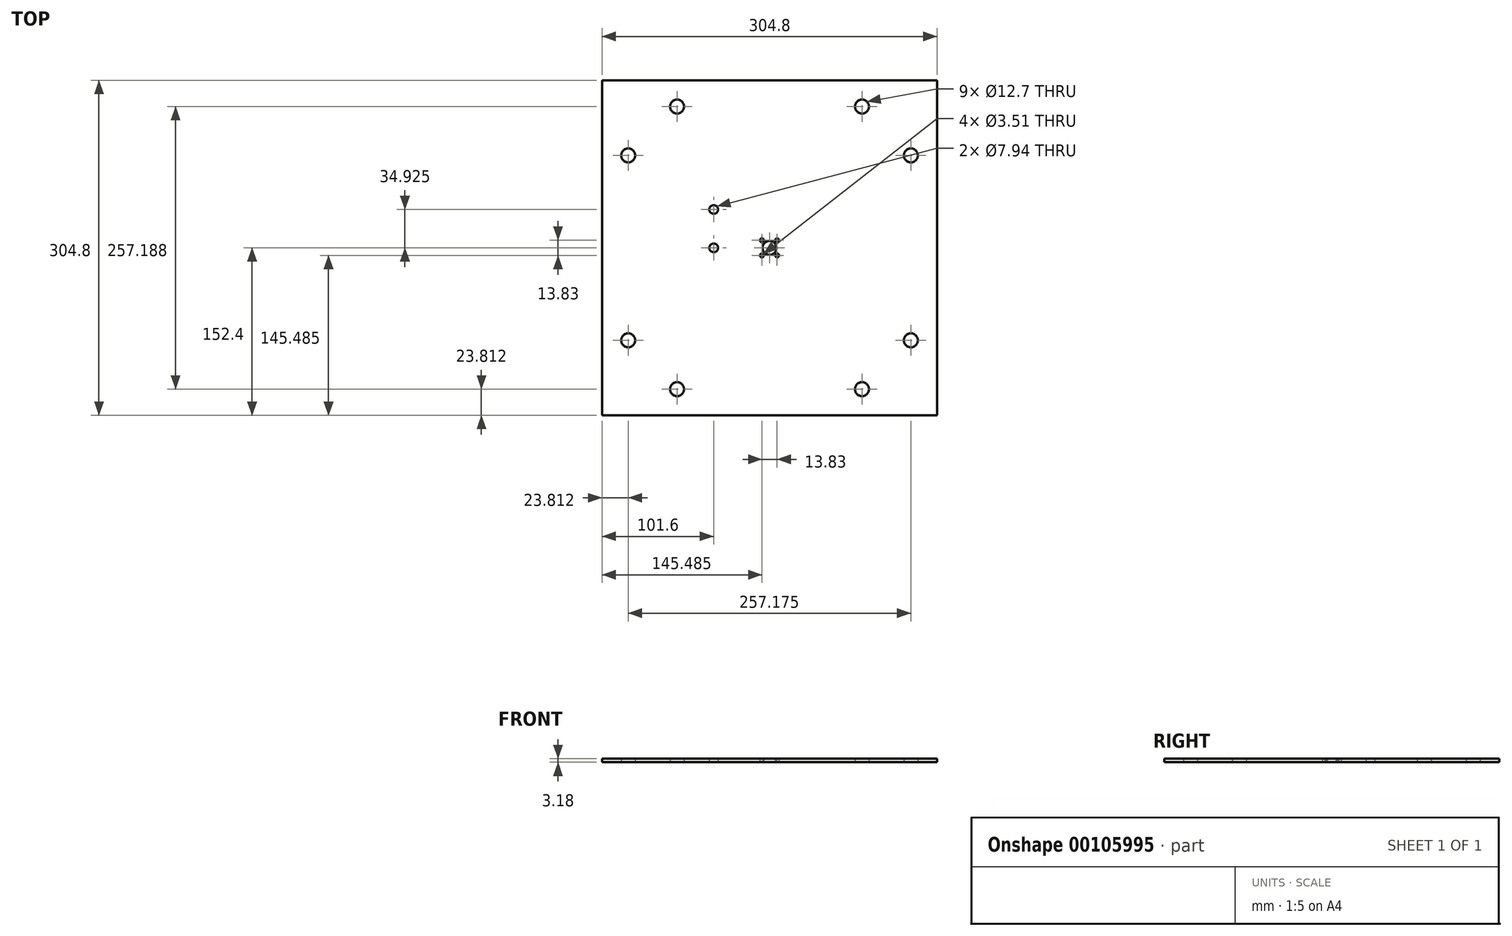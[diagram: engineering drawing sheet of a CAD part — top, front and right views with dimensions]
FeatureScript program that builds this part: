
annotation { "Feature Type Name" : "Feature", "Feature Type Description" : "" }
export const myFeature = defineFeature(function(context is Context, id is Id, definition is map)
    precondition{}
    {
        {
            var Q0;
            Q0=qCreatedBy(makeId("Top.planeOp"),FACE);
            var sketch = newSketch(context, id + "F0", { "sketchPlane" : qUnion([Q0])});
            skLineSegment(sketch, "E0.bottom", {"start": v(-152.4, 152.4) * mm, "end": v(152.4, 152.4) * mm});
            skLineSegment(sketch, "E0.top", {"start": v(-152.4, -152.4) * mm, "end": v(152.4, -152.4) * mm});
            skLineSegment(sketch, "E0.left", {"start": v(-152.4, 152.4) * mm, "end": v(-152.4, -152.4) * mm});
            skLineSegment(sketch, "E0.right", {"start": v(152.4, 152.4) * mm, "end": v(152.4, -152.4) * mm});
            skCircle(sketch, "E1", {"center": v(0, 0) * mm, "radius": 6.35 * mm});
            skLineSegment(sketch, "E2.bottom", {"start": v(-8.98, 8.98) * mm, "end": v(8.98, 8.98) * mm, "construction": true});
            skLineSegment(sketch, "E2.top", {"start": v(-8.98, -8.98) * mm, "end": v(8.98, -8.98) * mm, "construction": true});
            skLineSegment(sketch, "E2.left", {"start": v(-8.98, 8.98) * mm, "end": v(-8.98, -8.98) * mm, "construction": true});
            skLineSegment(sketch, "E2.right", {"start": v(8.98, 8.98) * mm, "end": v(8.98, -8.98) * mm, "construction": true});
            skLineSegment(sketch, "E3", {"start": v(0, 8.98) * mm, "end": v(0, -8.98) * mm, "construction": true});
            skLineSegment(sketch, "E4", {"start": v(-8.98, 0) * mm, "end": v(8.98, 0) * mm, "construction": true});
            skLineSegment(sketch, "E5.bottom", {"start": v(-6.91, 6.91) * mm, "end": v(6.91, 6.91) * mm, "construction": true});
            skLineSegment(sketch, "E5.top", {"start": v(-6.91, -6.91) * mm, "end": v(6.91, -6.91) * mm, "construction": true});
            skLineSegment(sketch, "E5.left", {"start": v(-6.91, 6.91) * mm, "end": v(-6.91, -6.91) * mm, "construction": true});
            skLineSegment(sketch, "E5.right", {"start": v(6.91, 6.91) * mm, "end": v(6.91, -6.91) * mm, "construction": true});
            skLineSegment(sketch, "E6", {"start": v(0, 6.91) * mm, "end": v(0, -6.91) * mm, "construction": true});
            skLineSegment(sketch, "E7", {"start": v(-6.91, 0) * mm, "end": v(6.91, 0) * mm, "construction": true});
            skCircle(sketch, "E8", {"center": v(-6.91, 6.91) * mm, "radius": 1.75 * mm});
            skCircle(sketch, "E9", {"center": v(6.91, 6.91) * mm, "radius": 1.75 * mm});
            skCircle(sketch, "E10", {"center": v(6.91, -6.91) * mm, "radius": 1.75 * mm});
            skCircle(sketch, "E11", {"center": v(-6.91, -6.91) * mm, "radius": 1.75 * mm});
            skLineSegment(sketch, "E12.bottom", {"start": v(-152.4, 152.4) * mm, "end": v(-128.59, 152.4) * mm, "construction": true});
            skLineSegment(sketch, "E12.top", {"start": v(-152.4, 128.59) * mm, "end": v(-128.59, 128.59) * mm, "construction": true});
            skLineSegment(sketch, "E12.left", {"start": v(-152.4, 152.4) * mm, "end": v(-152.4, 128.59) * mm, "construction": true});
            skLineSegment(sketch, "E12.right", {"start": v(-128.59, 152.4) * mm, "end": v(-128.59, 128.59) * mm, "construction": true});
            skLineSegment(sketch, "E13.bottom", {"start": v(152.4, 152.4) * mm, "end": v(128.59, 152.4) * mm, "construction": true});
            skLineSegment(sketch, "E13.top", {"start": v(152.4, 128.6) * mm, "end": v(128.59, 128.6) * mm, "construction": true});
            skLineSegment(sketch, "E13.left", {"start": v(152.4, 152.4) * mm, "end": v(152.4, 128.6) * mm, "construction": true});
            skLineSegment(sketch, "E13.right", {"start": v(128.59, 152.4) * mm, "end": v(128.59, 128.6) * mm, "construction": true});
            skLineSegment(sketch, "E14.bottom", {"start": v(152.4, -152.4) * mm, "end": v(128.59, -152.4) * mm, "construction": true});
            skLineSegment(sketch, "E14.top", {"start": v(152.4, -128.59) * mm, "end": v(128.59, -128.59) * mm, "construction": true});
            skLineSegment(sketch, "E14.left", {"start": v(152.4, -152.4) * mm, "end": v(152.4, -128.59) * mm, "construction": true});
            skLineSegment(sketch, "E14.right", {"start": v(128.59, -152.4) * mm, "end": v(128.59, -128.59) * mm, "construction": true});
            skLineSegment(sketch, "E15.bottom", {"start": v(-152.4, -152.4) * mm, "end": v(-128.59, -152.4) * mm, "construction": true});
            skLineSegment(sketch, "E15.top", {"start": v(-152.4, -128.59) * mm, "end": v(-128.59, -128.59) * mm, "construction": true});
            skLineSegment(sketch, "E15.left", {"start": v(-152.4, -152.4) * mm, "end": v(-152.4, -128.59) * mm, "construction": true});
            skLineSegment(sketch, "E15.right", {"start": v(-128.59, -152.4) * mm, "end": v(-128.59, -128.59) * mm, "construction": true});
            skLineSegment(sketch, "E16", {"start": v(-128.59, 152.4) * mm, "end": v(-128.59, 84.14) * mm, "construction": true});
            skLineSegment(sketch, "E17", {"start": v(-152.4, 128.59) * mm, "end": v(-84.14, 128.59) * mm, "construction": true});
            skLineSegment(sketch, "E18", {"start": v(152.4, 128.6) * mm, "end": v(84.14, 128.6) * mm, "construction": true});
            skLineSegment(sketch, "E19", {"start": v(128.59, 152.4) * mm, "end": v(128.59, 84.14) * mm, "construction": true});
            skLineSegment(sketch, "E20", {"start": v(128.59, -152.4) * mm, "end": v(128.59, -84.14) * mm, "construction": true});
            skLineSegment(sketch, "E21", {"start": v(152.4, -128.59) * mm, "end": v(84.13, -128.59) * mm, "construction": true});
            skLineSegment(sketch, "E22", {"start": v(-152.4, -128.59) * mm, "end": v(-84.14, -128.59) * mm, "construction": true});
            skLineSegment(sketch, "E23", {"start": v(-128.59, -152.4) * mm, "end": v(-128.59, -84.14) * mm, "construction": true});
            skCircle(sketch, "E24", {"center": v(-128.59, -84.14) * mm, "radius": 6.35 * mm, "construction": true});
            skCircle(sketch, "E25", {"center": v(-84.14, -128.59) * mm, "radius": 6.35 * mm, "construction": true});
            skCircle(sketch, "E26", {"center": v(-128.59, 84.14) * mm, "radius": 6.35 * mm});
            skCircle(sketch, "E27", {"center": v(-128.59, -84.14) * mm, "radius": 6.35 * mm});
            skCircle(sketch, "E28", {"center": v(-84.14, -128.59) * mm, "radius": 6.35 * mm});
            skCircle(sketch, "E29", {"center": v(84.13, -128.59) * mm, "radius": 6.35 * mm});
            skCircle(sketch, "E30", {"center": v(128.59, -84.14) * mm, "radius": 6.35 * mm});
            skCircle(sketch, "E31", {"center": v(128.59, 84.14) * mm, "radius": 6.35 * mm});
            skCircle(sketch, "E32", {"center": v(84.14, 128.6) * mm, "radius": 6.35 * mm});
            skCircle(sketch, "E33", {"center": v(-84.14, 128.59) * mm, "radius": 6.35 * mm});
            skLineSegment(sketch, "E34", {"start": v(0, -152.4) * mm, "end": v(-50.8, -152.4) * mm, "construction": true});
            skLineSegment(sketch, "E35", {"start": v(-50.8, -152.4) * mm, "end": v(-50.8, 0) * mm, "construction": true});
            skCircle(sketch, "E36", {"center": v(-50.8, 0) * mm, "radius": 3.97 * mm});
            skLineSegment(sketch, "E37", {"start": v(-50.8, -152.4) * mm, "end": v(-50.8, 34.92) * mm, "construction": true});
            skCircle(sketch, "E38", {"center": v(-50.8, 34.92) * mm, "radius": 3.97 * mm});
            skSolve(sketch);
        }
        {
            var Q0;
            Q0=makeQuery(id+"F0.imprint","IMPRINT",FACE,{"disambiguationData":[TD([[makeQuery(id+"F0.imprint","IMPRINT",EDGE,{"derivedFrom":sQuery(id+"F0.wireOp",EDGE,"E0.bottom")}),-1.0]])]});
            extrude(context, id + "F1", {"entities" : qUnion([Q0]), "depth" : 3.17 * mm});
        }
    });
